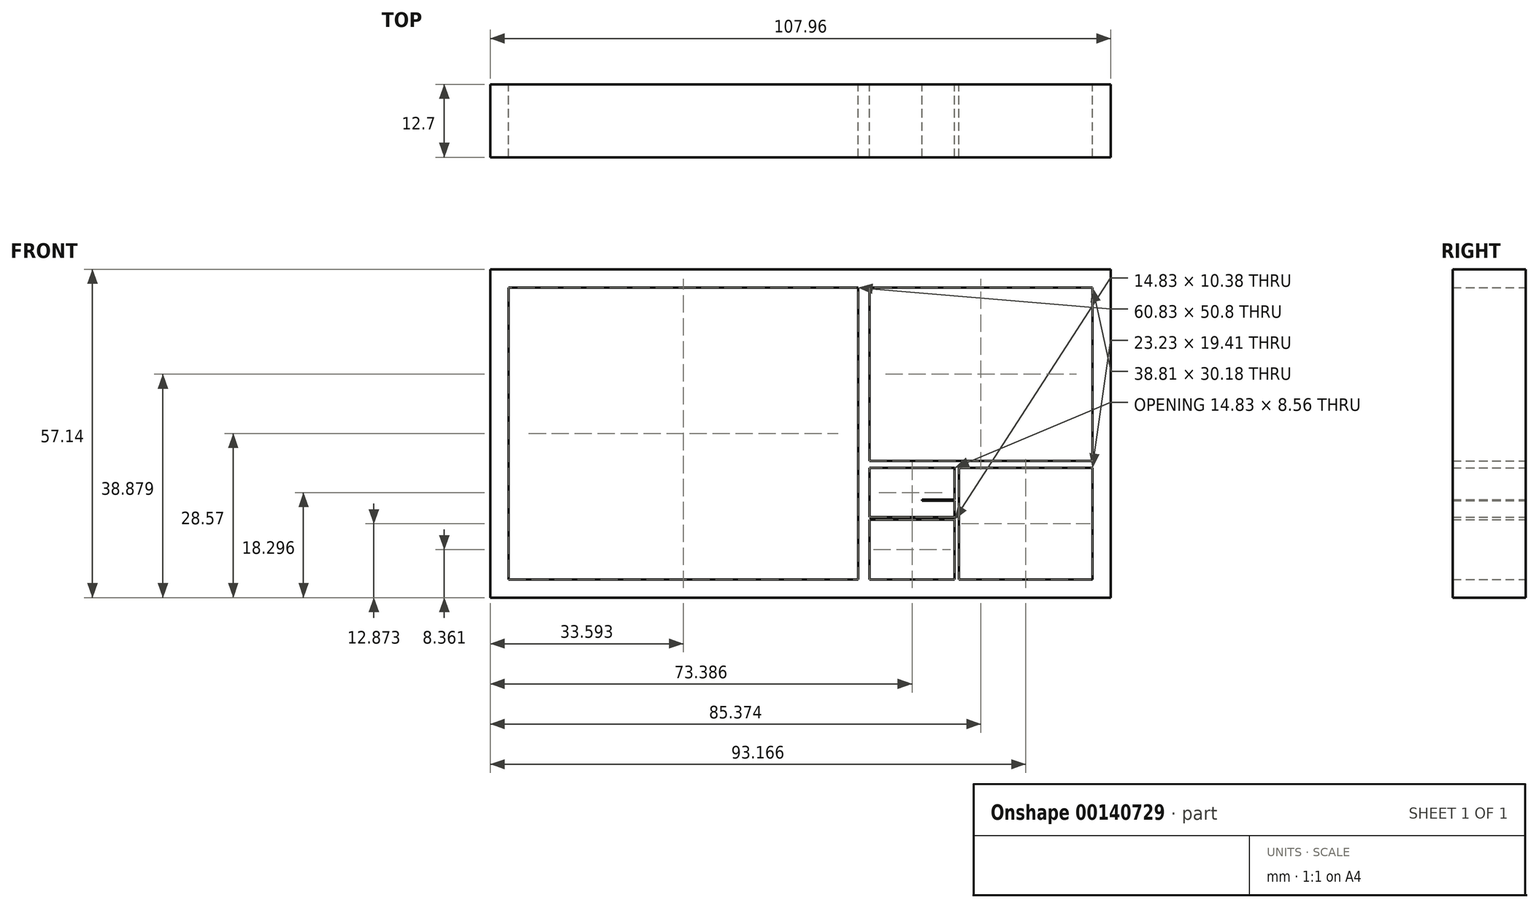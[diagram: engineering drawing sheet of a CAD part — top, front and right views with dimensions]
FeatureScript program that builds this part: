
annotation { "Feature Type Name" : "Feature", "Feature Type Description" : "" }
export const myFeature = defineFeature(function(context is Context, id is Id, definition is map)
    precondition{}
    {
        {
            var Q0;
            Q0=qCreatedBy(makeId("Front.planeOp"),FACE);
            var sketch = newSketch(context, id + "F0", { "sketchPlane" : qUnion([Q0])});
            skLineSegment(sketch, "E0.bottom", {"start": v(50.8, -25.4) * mm, "end": v(-50.8, -25.4) * mm});
            skLineSegment(sketch, "E0.top", {"start": v(50.8, 25.4) * mm, "end": v(-50.8, 25.4) * mm});
            skLineSegment(sketch, "E0.left", {"start": v(50.8, -25.4) * mm, "end": v(50.8, 25.4) * mm});
            skLineSegment(sketch, "E0.right", {"start": v(-50.8, -25.4) * mm, "end": v(-50.8, 25.4) * mm});
            skPoint(sketch, "E0.middle", {"position": v(0, 0) * mm});
            skLineSegment(sketch, "E1", {"start": v(-50.8, 25.4) * mm, "end": v(11.99, 25.4) * mm});
            skLineSegment(sketch, "E2", {"start": v(11.99, 25.4) * mm, "end": v(11.99, -25.4) * mm});
            skLineSegment(sketch, "E3", {"start": v(11.99, 25.4) * mm, "end": v(11.99, -6) * mm});
            skLineSegment(sketch, "E4", {"start": v(11.99, -6) * mm, "end": v(50.8, -6) * mm});
            skLineSegment(sketch, "E5", {"start": v(11.99, -25.4) * mm, "end": v(26.82, -25.4) * mm});
            skLineSegment(sketch, "E6", {"start": v(26.82, -25.4) * mm, "end": v(26.82, -6) * mm});
            skLineSegment(sketch, "E7", {"start": v(11.99, -25.4) * mm, "end": v(11.99, -14.55) * mm});
            skLineSegment(sketch, "E8", {"start": v(11.99, -14.55) * mm, "end": v(26.82, -14.55) * mm});
            skPoint(sketch, "E8.endSnap0", {"position": v(26.82, -15.7) * mm});
            skLineSegment(sketch, "E9", {"start": v(11.99, -14.55) * mm, "end": v(19.4, -14.55) * mm});
            skLineSegment(sketch, "E10", {"start": v(11.99, -14.55) * mm, "end": v(21.16, -14.55) * mm});
            skLineSegment(sketch, "E11", {"start": v(21.16, -14.55) * mm, "end": v(21.16, -6) * mm});
            skLineSegment(sketch, "E12", {"start": v(21.16, -14.55) * mm, "end": v(21.16, -11.7) * mm});
            skLineSegment(sketch, "E13", {"start": v(21.16, -11.7) * mm, "end": v(26.82, -11.7) * mm});
            skLineSegment(sketch, "E14.0", {"start": v(53.98, 28.58) * mm, "end": v(-53.98, 28.57) * mm});
            skLineSegment(sketch, "E14.1", {"start": v(53.98, -28.58) * mm, "end": v(53.98, 28.58) * mm});
            skLineSegment(sketch, "E14.2", {"start": v(53.98, -28.57) * mm, "end": v(-53.98, -28.58) * mm});
            skLineSegment(sketch, "E14.3", {"start": v(-53.98, -28.58) * mm, "end": v(-53.98, 28.57) * mm});
            skLineSegment(sketch, "E15.0", {"start": v(10.03, 25.4) * mm, "end": v(10.03, -25.4) * mm});
            skLineSegment(sketch, "E16.0", {"start": v(11.99, -4.78) * mm, "end": v(50.8, -4.78) * mm});
            skLineSegment(sketch, "E17.0", {"start": v(27.57, -25.4) * mm, "end": v(27.57, -6) * mm});
            skLineSegment(sketch, "E18.0", {"start": v(11.99, -15.02) * mm, "end": v(26.82, -15.02) * mm});
            skLineSegment(sketch, "E19.0", {"start": v(20.87, -14.55) * mm, "end": v(20.87, -6) * mm});
            skLineSegment(sketch, "E20.0", {"start": v(21.16, -11.53) * mm, "end": v(26.82, -11.53) * mm});
            skSolve(sketch);
        }
        {
            var Q0;
            {var subQ1=sQuery(id+"F0.wireOp",EDGE,"E0.top");Q0=makeQuery(id+"F0.imprint","IMPRINT",FACE,{"disambiguationData":[TD([[makeQuery(id+"F0.imprint","IMPRINT",EDGE,{"derivedFrom":subQ1}),-1.0]])]});}
            var Q1;
            {var subQ4=sQuery(id+"F0.wireOp",EDGE,"E2");Q1=makeQuery(id+"F0.imprint","IMPRINT",FACE,{"disambiguationData":[TD([[makeQuery(id+"F0.imprint","IMPRINT",EDGE,{"derivedFrom":subQ4}),-1.0]])]});}
            var Q2;
            {var subQ8=sQuery(id+"F0.wireOp",EDGE,"E16.0");Q2=makeQuery(id+"F0.imprint","IMPRINT",FACE,{"disambiguationData":[TD([[makeQuery(id+"F0.imprint","IMPRINT",EDGE,{"derivedFrom":subQ8}),-1.0]])]});}
            var Q3;
            {var subQ5=sQuery(id+"F0.wireOp",EDGE,"E17.0");Q3=makeQuery(id+"F0.imprint","IMPRINT",FACE,{"disambiguationData":[TD([[makeQuery(id+"F0.imprint","IMPRINT",EDGE,{"derivedFrom":subQ5}),1.0]])]});}
            var Q4;
            {var subQ4=sQuery(id+"F0.wireOp",EDGE,"E8");Q4=makeQuery(id+"F0.imprint","IMPRINT",FACE,{"disambiguationData":[TD([[makeQuery(id+"F0.imprint","IMPRINT",EDGE,{"derivedFrom":subQ4}),-1.0]])]});}
            var Q5;
            {var subQ4=sQuery(id+"F0.wireOp",EDGE,"E12");Q5=makeQuery(id+"F0.imprint","IMPRINT",FACE,{"disambiguationData":[TD([[makeQuery(id+"F0.imprint","IMPRINT",EDGE,{"derivedFrom":subQ4}),1.0]])]});}
            var Q6;
            {var subQ0=sQuery(id+"F0.wireOp",EDGE,"E13");Q6=makeQuery(id+"F0.imprint","IMPRINT",FACE,{"disambiguationData":[TD([[makeQuery(id+"F0.imprint","IMPRINT",EDGE,{"derivedFrom":subQ0}),1.0]])]});}
            extrude(context, id + "F1", {"entities" : qUnion([Q0, Q1, Q2, Q3, Q4, Q5, Q6]), "depth" : 12.7 * mm});
        }
    });
